# Revit family: LVS
name_source: partatom
category: Communication Devices
units: mm (PartAtom-declared; Revit-internal decimal feet)

## family parameters
Cut with Voids When Loaded = No
Host = Face
Maintain Annotation Orientation = No
OmniClass Number = 23.85.80.11.27
OmniClass Title = Lighting Controls
Part Type = Normal
Room Calculation Point = No
Round Connector Dimension = Use Diameter
Shared = Yes

## types (1)
- LVS
    Assembly Code = D5090
    Default Elevation = 48 "
    Description = Low Voltage Emergency Remote Test Button
    Environmental Conditions = • Rated for Indoor Use Only
• Operating Temperature: -4° to 131°F
(-20° to 55°C)
• Relative humidity (non-condensing):0 to 95%
    Feartures = Attractive Flush mount design
• Stainless Steel Latching button
• Optional illuminated pilot button
• Low Voltage 24VDC
• Wall plate factory labeled
• Compatible for use with select HCS Emergency controls:
ALCR1277 and NXRC-UL924-UNV*
    Height = 4.94 "
    Housing Material = Paint -  Light Silver
    Manufacturer = NX Lighting Controls
    Model = LVS
    Steel = Metal-Galvanized_Steel
    Type Comments = Low Voltage Emergency Remote Test Button
    URL = https://www.currentlighting.com
    Warranty = 5-Years Warranty
    Width = 3.15 "

## geometry (parser evidence)
native form markers: Sweep x3
no freeform markers — native parametric forms only
